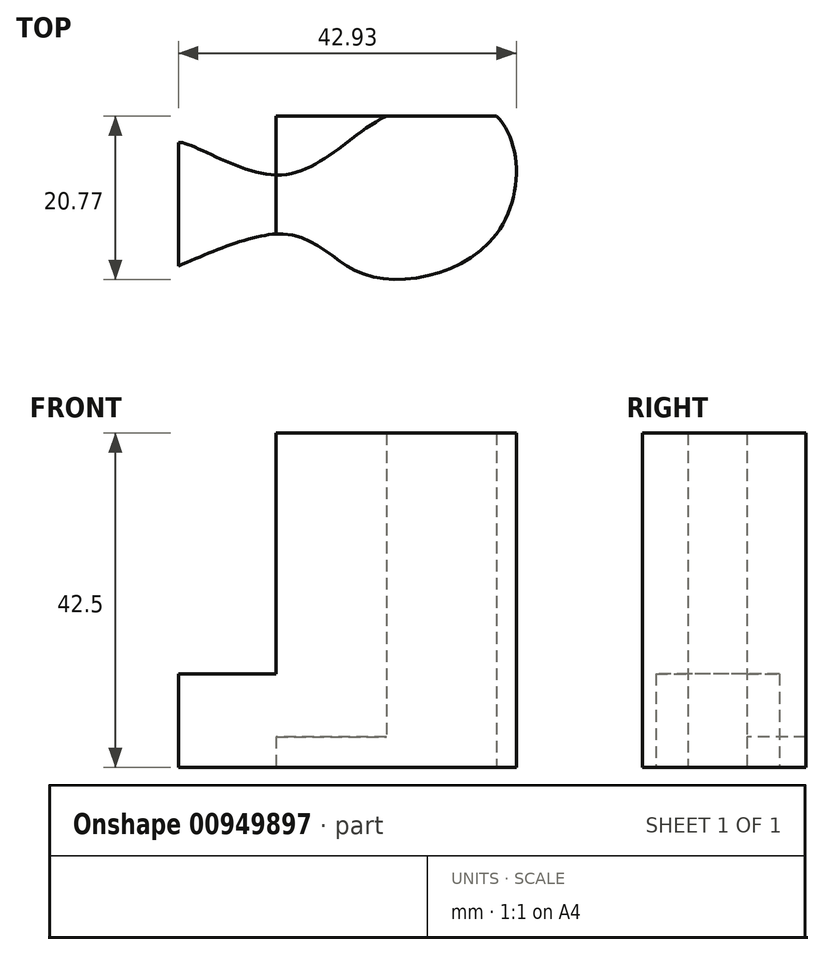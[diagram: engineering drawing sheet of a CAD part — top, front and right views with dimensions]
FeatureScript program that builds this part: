
annotation { "Feature Type Name" : "Feature", "Feature Type Description" : "" }
export const myFeature = defineFeature(function(context is Context, id is Id, definition is map)
    precondition{}
    {
        {
            var Q0;
            Q0=qCreatedBy(makeId("Top.planeOp"),FACE);
            var sketch = newSketch(context, id + "F0", { "sketchPlane" : qUnion([Q0])});
            skLineSegment(sketch, "E0.bottom", {"start": v(1.21, -1) * mm, "end": v(29.21, -1) * mm});
            skLineSegment(sketch, "E0.top", {"start": v(1.21, -16) * mm, "end": v(29.21, -16) * mm});
            skLineSegment(sketch, "E0.left", {"start": v(1.21, -1) * mm, "end": v(1.21, -16) * mm});
            skLineSegment(sketch, "E0.right", {"start": v(29.21, -1) * mm, "end": v(29.21, -16) * mm});
            skPoint(sketch, "E1.8.internal.snap0", {"position": v(1.21, -8.5) * mm});
            skFitSpline(sketch, "E1", {"points": [v(-18.07, -21.9) * mm, v(1.21, -16) * mm, v(12.6, -21.18) * mm, v(29.21, -16) * mm, v(29.21, -1) * mm, v(15.21, -1) * mm, v(1.21, -8.5) * mm, v(-11.2, -4.37) * mm, v(-12.5, -8.5) * mm, v(-18.07, -21.9) * mm]});
            skFitSpline(sketch, "E2", {"points": [v(-23.52, -22.6) * mm, v(-13.92, -34.8) * mm, v(0, -27.22) * mm, v(7.04, -39.3) * mm, v(-13.57, -38.6) * mm, v(-25.41, -48.3) * mm, v(-23.52, -22.6) * mm]});
            skLineSegment(sketch, "E3.left", {"start": v(-11.2, -4.37) * mm, "end": v(-11.2, -20.06) * mm});
            skSolve(sketch);
        }
        {
            var Q0;
            {var subQ0=sQuery(id+"F0.wireOp",EDGE,"E0.left");var subQ1=sQuery(id+"F0.wireOp",EDGE,"E0.bottom");var subQ2=makeQuery(id+"F0.imprint","INTERSECT",VERTEX,{"derivedFrom":[subQ1,subQ0]});Q0=makeQuery(id+"F0.imprint","IMPRINT",FACE,{"disambiguationData":[TD([[makeQuery(id+"F0.imprint","IMPRINT",EDGE,{"disambiguationData":[TD([[subQ2,-1.0]])],"derivedFrom":subQ1}),-1.0]])]});}
            var Q1;
            {var subQ5=sQuery(id+"F0.wireOp",EDGE,"E0.right");Q1=makeQuery(id+"F0.imprint","IMPRINT",FACE,{"disambiguationData":[TD([[makeQuery(id+"F0.imprint","IMPRINT",EDGE,{"derivedFrom":subQ5}),-1.0]])]});}
            extrude(context, id + "F1", {"entities" : qUnion([Q0, Q1]), "depth" : 3.9 * mm, "offsetDistance" : 25 * mm});
        }
        {
            var Q0;
            {var subQ4=sQuery(id+"F0.wireOp",EDGE,"E3.left");Q0=makeQuery(id+"F0.imprint","IMPRINT",FACE,{"disambiguationData":[TD([[makeQuery(id+"F0.imprint","IMPRINT",EDGE,{"derivedFrom":subQ4}),1.0]])]});}
            extrude(context, id + "F2", {"entities" : qUnion([Q0]), "operationType" : NewBodyOperationType.ADD, "depth" : 11.9 * mm, "offsetDistance" : 25 * mm});
        }
        {
            var Q0;
            {var subQ0=sQuery(id+"F0.wireOp",EDGE,"E1");var subQ1=sQuery(id+"F0.wireOp",EDGE,"E0.top");var subQ3=makeQuery(id+"F0.imprint","INTERSECT",VERTEX,{"derivedFrom":[subQ1,subQ0]});Q0=makeQuery(id+"F0.imprint","IMPRINT",FACE,{"disambiguationData":[TD([[makeQuery(id+"F0.imprint","IMPRINT",EDGE,{"disambiguationData":[TD([[subQ3,-1.0]])],"derivedFrom":subQ1}),-1.0]])]});}
            var Q1;
            {var subQ5=sQuery(id+"F0.wireOp",EDGE,"E0.right");Q1=makeQuery(id+"F0.imprint","IMPRINT",FACE,{"disambiguationData":[TD([[makeQuery(id+"F0.imprint","IMPRINT",EDGE,{"derivedFrom":subQ5}),-1.0]])]});}
            var Q2;
            {var subQ0=sQuery(id+"F0.wireOp",EDGE,"E0.right");Q2=makeQuery(id+"F0.imprint","IMPRINT",FACE,{"disambiguationData":[TD([[makeQuery(id+"F0.imprint","IMPRINT",EDGE,{"derivedFrom":subQ0}),1.0]])]});}
            extrude(context, id + "F3", {"entities" : qUnion([Q0, Q1, Q2]), "operationType" : NewBodyOperationType.ADD, "depth" : 42.5 * mm, "offsetDistance" : 25 * mm});
        }
    });
